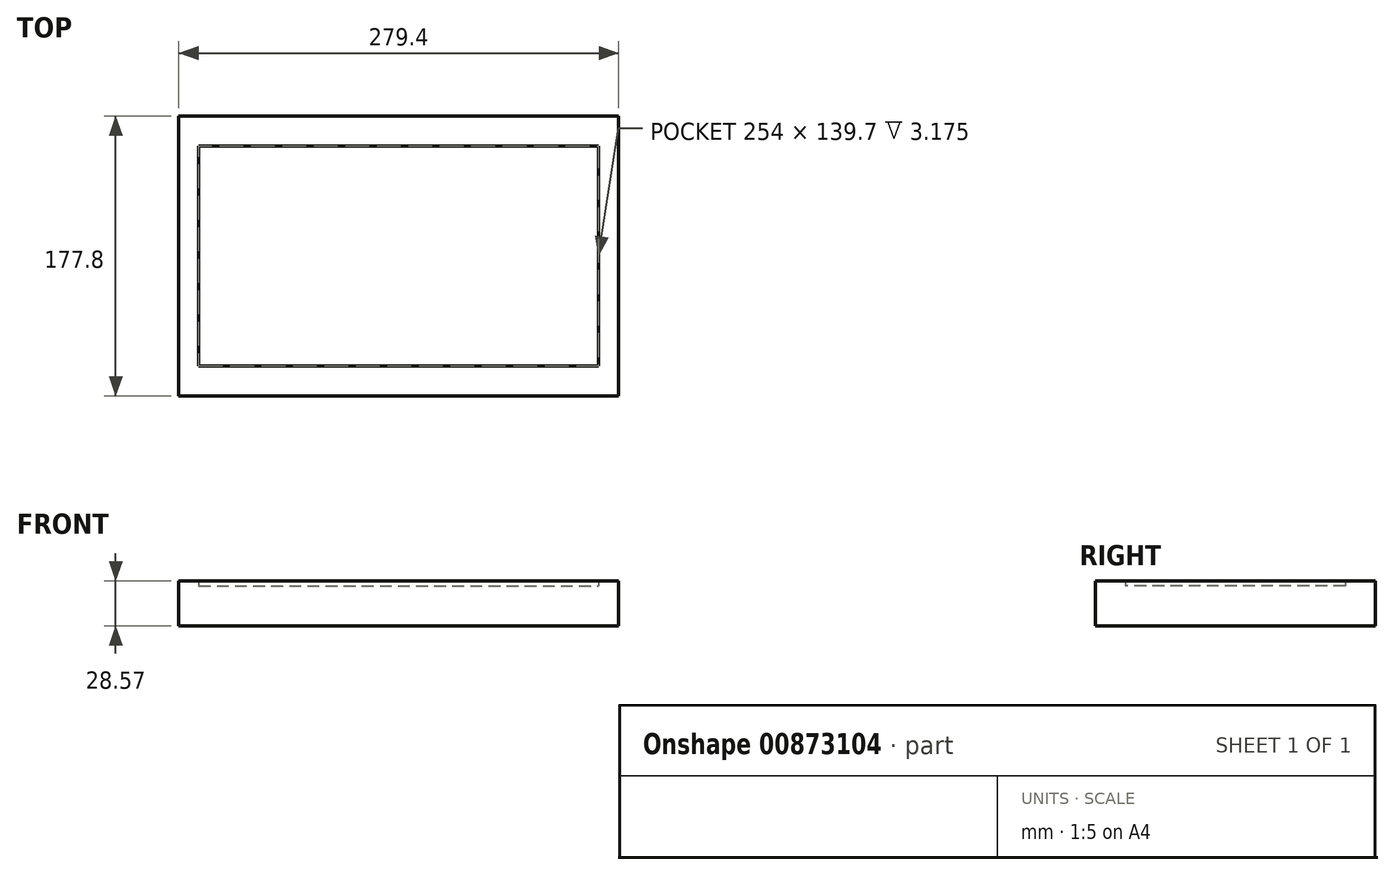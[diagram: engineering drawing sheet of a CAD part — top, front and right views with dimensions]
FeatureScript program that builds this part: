
annotation { "Feature Type Name" : "Feature", "Feature Type Description" : "" }
export const myFeature = defineFeature(function(context is Context, id is Id, definition is map)
    precondition{}
    {
        {
            var Q0;
            Q0=qCreatedBy(makeId("Top.planeOp"),FACE);
            var sketch = newSketch(context, id + "F0", { "sketchPlane" : qUnion([Q0])});
            skLineSegment(sketch, "E0.bottom", {"start": v(-127, 69.85) * mm, "end": v(127, 69.85) * mm});
            skLineSegment(sketch, "E0.top", {"start": v(-127, -69.85) * mm, "end": v(127, -69.85) * mm});
            skLineSegment(sketch, "E0.left", {"start": v(-127, 69.85) * mm, "end": v(-127, -69.85) * mm});
            skLineSegment(sketch, "E0.right", {"start": v(127, 69.85) * mm, "end": v(127, -69.85) * mm});
            skPoint(sketch, "E0.middle", {"position": v(0, 0) * mm});
            skLineSegment(sketch, "E1.bottom", {"start": v(139.7, -88.9) * mm, "end": v(-139.7, -88.9) * mm});
            skLineSegment(sketch, "E1.top", {"start": v(139.7, 88.9) * mm, "end": v(-139.7, 88.9) * mm});
            skLineSegment(sketch, "E1.left", {"start": v(139.7, -88.9) * mm, "end": v(139.7, 88.9) * mm});
            skLineSegment(sketch, "E1.right", {"start": v(-139.7, -88.9) * mm, "end": v(-139.7, 88.9) * mm});
            skSolve(sketch);
        }
        {
            var Q0;
            Q0 = qSketchRegion(id + "F0", true);
            extrude(context, id + "F1", {"entities" : qUnion([Q0]), "depth" : 3.17 * mm, "offsetDistance" : 25.4 * mm});
        }
        {
            var Q0;
            Q0=makeQuery(id+"F1.opExtrude","CAP_FACE",FACE,{"disambiguationData":[OSD([sQuery(id+"F0.wireOp",EDGE,"E0.bottom"),sQuery(id+"F0.wireOp",EDGE,"E0.top"),sQuery(id+"F0.wireOp",EDGE,"E0.left"),sQuery(id+"F0.wireOp",EDGE,"E0.right"),sQuery(id+"F0.wireOp",EDGE,"E1.bottom"),sQuery(id+"F0.wireOp",EDGE,"E1.top"),sQuery(id+"F0.wireOp",EDGE,"E1.left"),sQuery(id+"F0.wireOp",EDGE,"E1.right")])],"isStart":true});
            var sketch = newSketch(context, id + "F2", { "sketchPlane" : qUnion([Q0])});
            skLineSegment(sketch, "E2.0", {"start": v(139.7, 88.9) * mm, "end": v(-139.7, 88.9) * mm});
            skLineSegment(sketch, "E3.0", {"start": v(-139.7, 88.9) * mm, "end": v(-139.7, -88.9) * mm});
            skLineSegment(sketch, "E3.1", {"start": v(139.7, -88.9) * mm, "end": v(-139.7, -88.9) * mm});
            skLineSegment(sketch, "E3.2", {"start": v(139.7, 88.9) * mm, "end": v(139.7, -88.9) * mm});
            skSolve(sketch);
        }
        {
            var Q0;
            Q0 = qSketchRegion(id + "F2", true);
            extrude(context, id + "F3", {"entities" : qUnion([Q0]), "operationType" : NewBodyOperationType.ADD, "depth" : 25.4 * mm, "offsetDistance" : 25.4 * mm});
        }
    });
